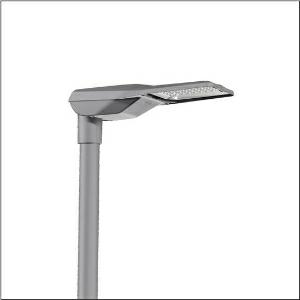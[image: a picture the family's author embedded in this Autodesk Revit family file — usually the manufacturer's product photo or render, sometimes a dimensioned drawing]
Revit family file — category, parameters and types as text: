
# Revit family: streetlight_sl_21_iq_mini___st1_0a_5xe2d41g08jb_4fff
name_source: partatom
category: Lighting Fixtures
units: mm (PartAtom-declared; Revit-internal decimal feet)

## family parameters
Cut with Voids When Loaded = No
Host = Face
Light Source = No
Part Type = Normal
Room Calculation Point = No
Round Connector Dimension = Use Diameter
Shared = No

## types (1)
- --- (1 x LED, 11290 lm, 71.6 W, 4000K)
    Apparent Load = 72 VA
    CIE Flux Codes = 40 73 97 100 100
    Color Rendering = 70
    Color Temperature = 4000K
    Default Elevation = 1800 mm
    Description = Streetlight SL 21 iQ mini, mast luminaire, primary light control with lens, of PMMA, primary optical cover: cover, of toughened safety glass, transparent, light distribution: ST1.0a, light emission: direct distribution, primary light characteristic: asymmetric, installation type: post-top, side-entry, LED, High Power LED, rated luminous flux: 11.290lm, luminous efficacy: 158lm/W, light colour: 740, colour temperature: 4000K, control gear: iQ Street-Remote, control: Street-Remote, Auto-Match, Temp-Guard, Lumen-Switch, Night-Set, Smart-Wire, Light-Fading, Desk-Remote (wireless, voltage-free reading and setting of iQ features in the workshop via application-optimized NFC function/RFID function), optimised constant luminous flux control (CLO 2.0), pre-setting: linear dimming characteristic, mains connection: 220..240V, AC, 50/60Hz, start of lifetime: 72W, end of service life: 75W, reduction: 33W, luminaire housing, of diecast aluminium, powder-coated, SITECO metallic grey (DB 702S), corrosivity category C5 high according to DIN EN ISO 12944, please order mast flange separately, inclination adjustable: 0°, 5°, 10°, 15°, sealing non-destructively replaceable, multi-level sealing system, length: 628mm, width: 235mm, height: 110mm, mast flange for spigot size: 42mm (side-entry): 5XC10008XM4, 60/48mm (side-entry/post-top): 5XC10108XM2, 76/60mm (side-entry/post-top): 5XC10108XM1, mounting height: 4..8m, protection rating (complete): IP66, insulation class (complete): insulation class II (safety insulation), certification: CE, ENEC, ENEC+, VDE, impact resistance: IK10, permissible operating ambient temperature for outdoor applications: -40..+50°C, standard-compliant lighting for roads and squares, packaging unit: 1 piece

Light Distribution: ST1.0a
    Height = 110 mm
    Lamp = 1 x LED
    Lamp Light Flux = 11290 lm
    Lamp Power = 71.6 W
    Lamp count = 1
    Length = 625 mm
    Luminous efficacy = 158 lm/W
    Manufacturer = Siteco
    ModVariant = No
    Model = 5XE2D41G08JB
    Number of Poles = 1
    OnlyDefault = Yes
    Power Factor = 1
    Product Name = Streetlight SL 21 iQ mini | ST1.0a
    Product group = mast luminaire | pylon top
    ProductGroupID = 6100
    Protection Class = Protection class II
    Protection Degree = IP 66
    RLX_Detail_Level = 1
    RLX_Emergency_Light_Flux = 0 lm
    RLX_Emergency_Type = 0
    RLX_Emergency_Type_DB = No
    RlxData = <blob elided: 26337 chars, md5=5a0241fb>
    Socket = socket
    Standby Power = 0 W
    System Light Flux = 11290 lm
    System Power = 72 W
    Type Comments = factory setting: luminous flux: 100 % | dim-lin: 254 | 746 mA
    Type Image = l_1003519.jpg
    URL = http://relux.com
    VarID = @adj_170563
    Voltage = 0 V
    Weight = 0.00 kg
    Width = 234 mm

## geometry (parser evidence)
native form markers: Blend x4, Sweep x11
no freeform markers — native parametric forms only
